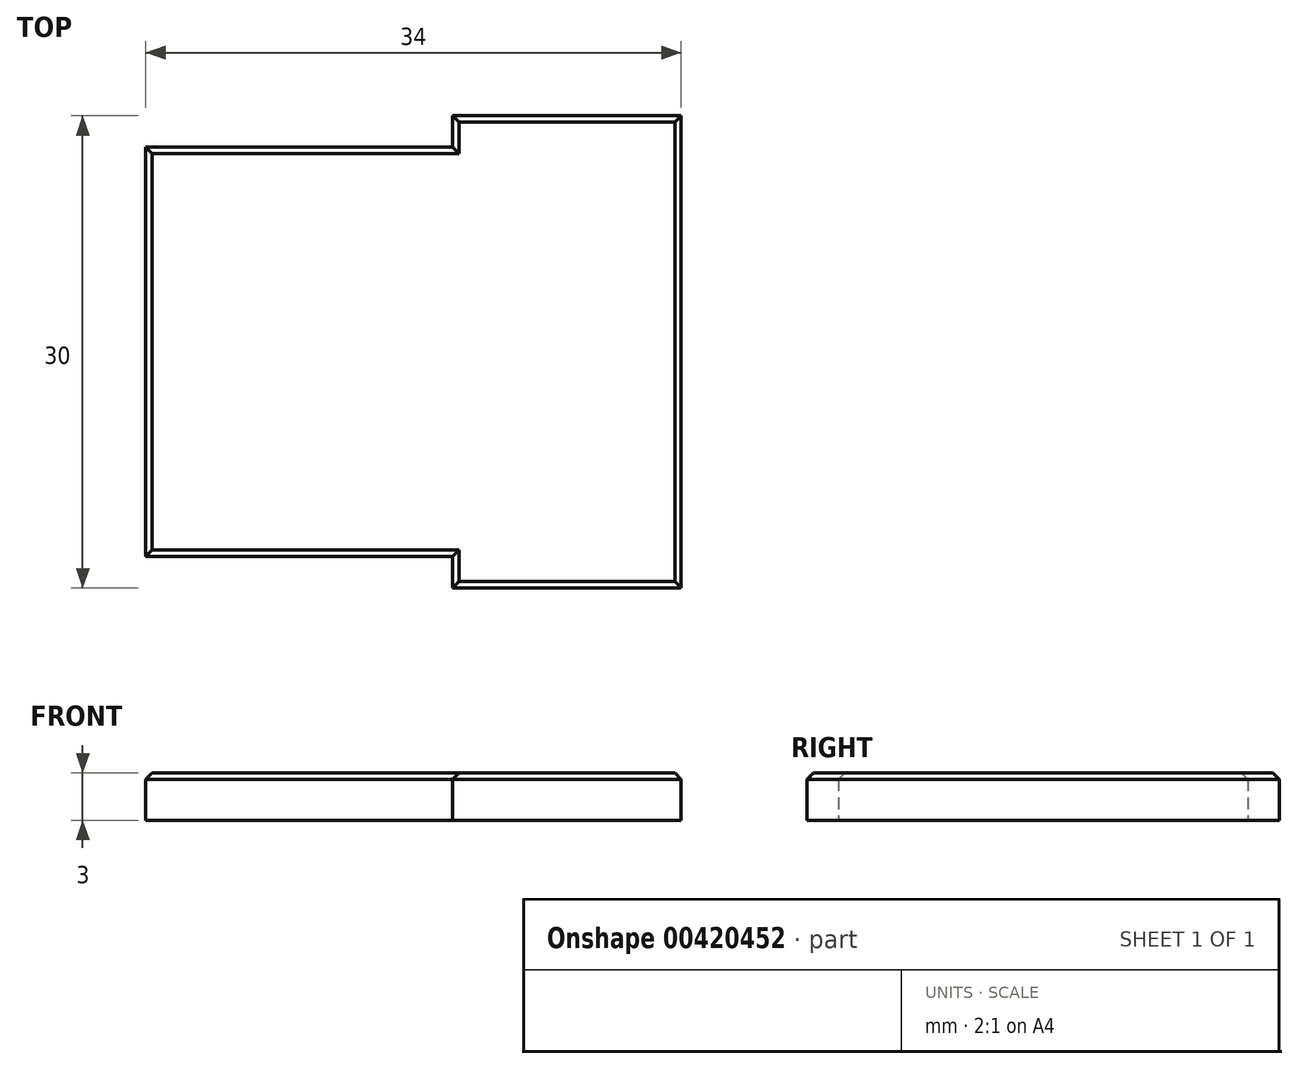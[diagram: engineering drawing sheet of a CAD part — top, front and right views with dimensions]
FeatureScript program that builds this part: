
annotation { "Feature Type Name" : "Feature", "Feature Type Description" : "" }
export const myFeature = defineFeature(function(context is Context, id is Id, definition is map)
    precondition{}
    {
        {
            var Q0;
            Q0=qCreatedBy(makeId("Top.planeOp"),FACE);
            var sketch = newSketch(context, id + "F0", { "sketchPlane" : qUnion([Q0])});
            skLineSegment(sketch, "E0.bottom", {"start": v(9.75, -13) * mm, "end": v(-9.75, -13) * mm});
            skLineSegment(sketch, "E0.top", {"start": v(9.75, 13) * mm, "end": v(-9.75, 13) * mm});
            skLineSegment(sketch, "E0.right", {"start": v(-9.75, -13) * mm, "end": v(-9.75, 13) * mm});
            skPoint(sketch, "E0.middle", {"position": v(0, 0) * mm});
            skLineSegment(sketch, "E1.bottom", {"start": v(9.75, -15) * mm, "end": v(24.25, -15) * mm});
            skLineSegment(sketch, "E1.top", {"start": v(9.75, 15) * mm, "end": v(24.25, 15) * mm});
            skLineSegment(sketch, "E1.left", {"start": v(9.75, -15) * mm, "end": v(9.75, -13) * mm});
            skLineSegment(sketch, "E1.right", {"start": v(24.25, -15) * mm, "end": v(24.25, 15) * mm});
            skPoint(sketch, "E1.middle", {"position": v(17, 0) * mm});
            skLineSegment(sketch, "E2.trimOffspring", {"start": v(9.75, 13) * mm, "end": v(9.75, 15) * mm});
            skSolve(sketch);
        }
        {
            var Q0;
            Q0=makeQuery(id+"F0.imprint","IMPRINT",FACE,{"disambiguationData":[TD([[makeQuery(id+"F0.imprint","IMPRINT",EDGE,{"derivedFrom":sQuery(id+"F0.wireOp",EDGE,"E0.bottom")}),-1.0]])]});
            extrude(context, id + "F1", {"entities" : qUnion([Q0]), "depth" : 3 * mm});
        }
        {
            var Q0;
            Q0=makeQuery(id+"F1.opExtrude","CAP_FACE",FACE,{"disambiguationData":[OSD([sQuery(id+"F0.wireOp",EDGE,"E0.bottom"),sQuery(id+"F0.wireOp",EDGE,"E0.top"),sQuery(id+"F0.wireOp",EDGE,"E0.right"),sQuery(id+"F0.wireOp",EDGE,"E1.bottom"),sQuery(id+"F0.wireOp",EDGE,"E1.top"),sQuery(id+"F0.wireOp",EDGE,"E1.left"),sQuery(id+"F0.wireOp",EDGE,"E1.right"),sQuery(id+"F0.wireOp",EDGE,"E2.trimOffspring")])],"isStart":false});
            chamfer(context, id + "F2", {"entities" : qUnion([Q0]), "width" : .4 * mm, "tangentPropagation" : true});
        }
    });
